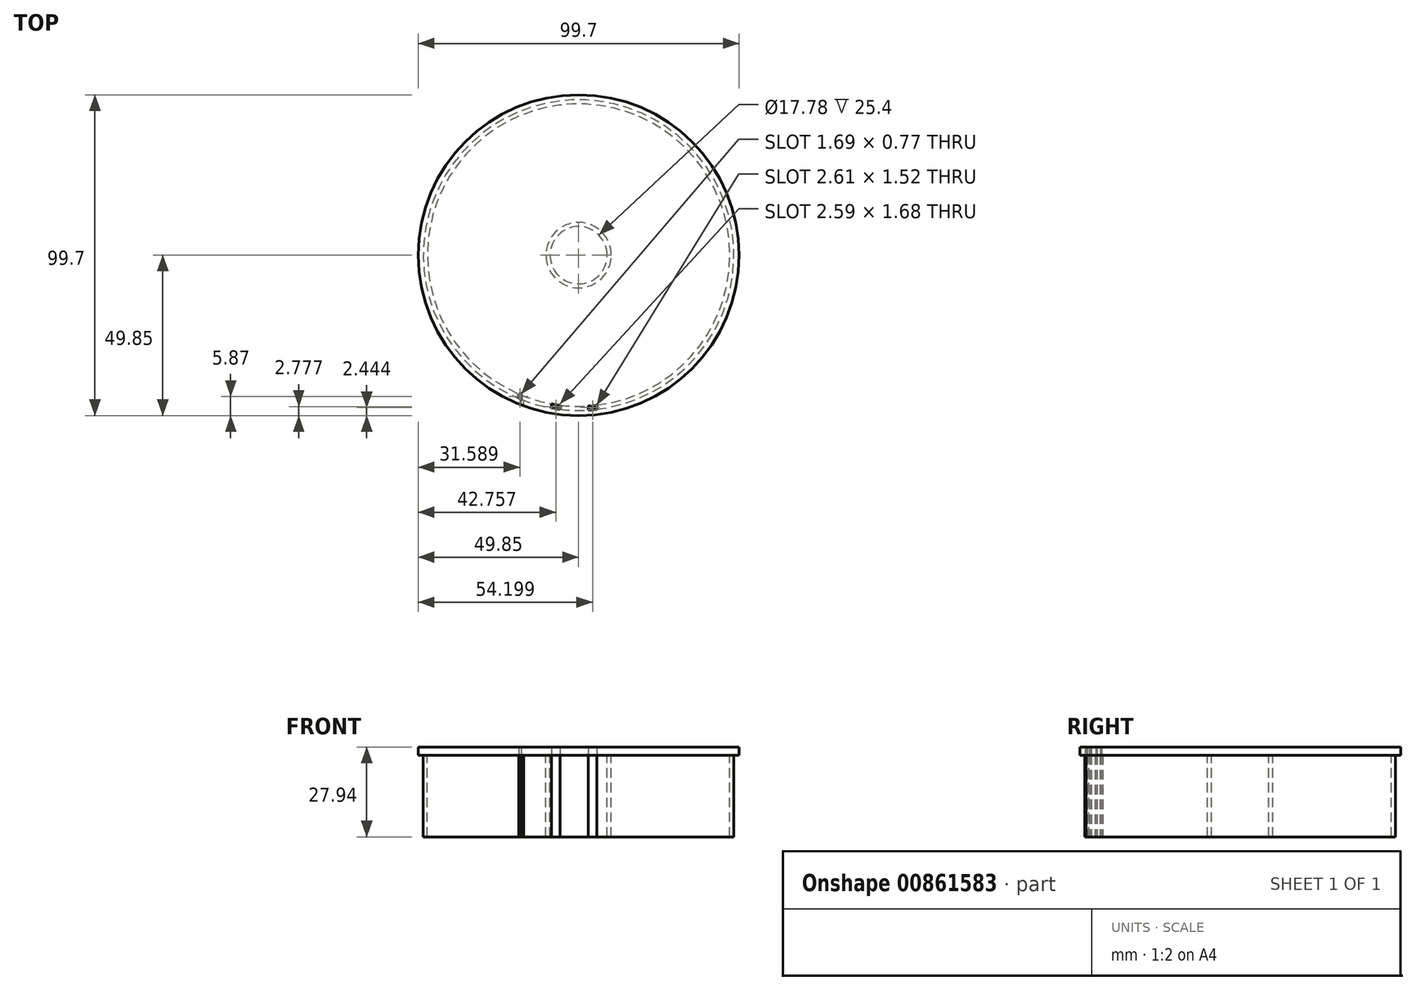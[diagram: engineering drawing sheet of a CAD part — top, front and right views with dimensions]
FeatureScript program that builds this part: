
annotation { "Feature Type Name" : "Feature", "Feature Type Description" : "" }
export const myFeature = defineFeature(function(context is Context, id is Id, definition is map)
    precondition{}
    {
        {
            var Q0;
            Q0=qCreatedBy(makeId("Top.planeOp"),FACE);
            var sketch = newSketch(context, id + "F0", { "sketchPlane" : qUnion([Q0])});
            skCircle(sketch, "E0", {"center": v(0, 0) * mm, "radius": 10.16 * mm});
            skCircle(sketch, "E1", {"center": v(0, 0) * mm, "radius": 48.26 * mm});
            skCircle(sketch, "E2", {"center": v(0, 0) * mm, "radius": 8.9 * mm});
            skCircle(sketch, "E3", {"center": v(0, 0) * mm, "radius": 47 * mm});
            skSolve(sketch);
        }
        {
            var Q0;
            Q0=makeQuery(id+"F0.imprint","IMPRINT",FACE,{"disambiguationData":[TD([[makeQuery(id+"F0.imprint","IMPRINT",EDGE,{"derivedFrom":sQuery(id+"F0.wireOp",EDGE,"E0")}),1.0]])]});
            var Q1;
            Q1=makeQuery(id+"F0.imprint","IMPRINT",FACE,{"disambiguationData":[TD([[makeQuery(id+"F0.imprint","IMPRINT",EDGE,{"derivedFrom":sQuery(id+"F0.wireOp",EDGE,"E1")}),1.0]])]});
            extrude(context, id + "F1", {"entities" : qUnion([Q0, Q1]), "oppositeDirection" : true, "depth" : 25.4 * mm, "offsetDistance" : 25.4 * mm});
        }
        {
            var Q0;
            Q0=qCreatedBy(makeId("Top.planeOp"),FACE);
            var sketch = newSketch(context, id + "F2", { "sketchPlane" : qUnion([Q0])});
            skCircle(sketch, "E4", {"center": v(0, 0) * mm, "radius": 49.85 * mm});
            skSolve(sketch);
        }
        {
            var Q0;
            Q0=makeQuery(id+"F2.imprint","IMPRINT",FACE,{"disambiguationData":[TD([[makeQuery(id+"F2.imprint","IMPRINT",EDGE,{"derivedFrom":sQuery(id+"F2.wireOp",EDGE,"E4")}),1.0]])]});
            extrude(context, id + "F3", {"entities" : qUnion([Q0]), "depth" : 2.54 * mm, "offsetDistance" : 25.4 * mm});
        }
        {
            var Q0;
            Q0=makeQuery(id+"F1.opExtrude","CAP_FACE",FACE,{"disambiguationData":[OSD([sQuery(id+"F0.wireOp",EDGE,"E1"),sQuery(id+"F0.wireOp",EDGE,"E3")])],"isStart":false});
            var sketch = newSketch(context, id + "F4", { "sketchPlane" : qUnion([Q0])});
            skLineSegment(sketch, "E5", {"start": v(-18.64, 44.51) * mm, "end": v(-18.64, 43.13) * mm});
            skLineSegment(sketch, "E6", {"start": v(-17.88, 44.83) * mm, "end": v(-17.88, 43.46) * mm});
            skLineSegment(sketch, "E7", {"start": v(-17.88, 43.46) * mm, "end": v(-18.64, 43.13) * mm});
            skLineSegment(sketch, "E8", {"start": v(-8.39, 47.53) * mm, "end": v(-8.39, 46.23) * mm});
            skLineSegment(sketch, "E9", {"start": v(-8.39, 46.23) * mm, "end": v(-5.8, 46.63) * mm});
            skLineSegment(sketch, "E10", {"start": v(-5.8, 46.63) * mm, "end": v(-5.8, 47.91) * mm});
            skLineSegment(sketch, "E11", {"start": v(-5.8, 47.91) * mm, "end": v(-8.39, 47.53) * mm});
            skLineSegment(sketch, "E12", {"start": v(3.04, 48.16) * mm, "end": v(3.04, 46.9) * mm});
            skLineSegment(sketch, "E13", {"start": v(3.04, 46.9) * mm, "end": v(5.66, 46.65) * mm});
            skLineSegment(sketch, "E14", {"start": v(5.66, 46.65) * mm, "end": v(5.66, 47.93) * mm});
            skLineSegment(sketch, "E15", {"start": v(5.66, 47.93) * mm, "end": v(3.04, 48.16) * mm});
            skSolve(sketch);
        }
        {
            var Q0;
            {var subQ0=sQuery(id+"F4.wireOp",EDGE,"E5");Q0=makeQuery(id+"F4.imprint","IMPRINT",FACE,{"disambiguationData":[TD([[makeQuery(id+"F4.imprint","IMPRINT",EDGE,{"derivedFrom":subQ0}),1.0]])]});}
            var Q1;
            {var subQ0=sQuery(id+"F4.wireOp",EDGE,"E8");Q1=makeQuery(id+"F4.imprint","IMPRINT",FACE,{"disambiguationData":[TD([[makeQuery(id+"F4.imprint","IMPRINT",EDGE,{"derivedFrom":subQ0}),1.0]])]});}
            var Q2;
            {var subQ0=sQuery(id+"F4.wireOp",EDGE,"E12");Q2=makeQuery(id+"F4.imprint","IMPRINT",FACE,{"disambiguationData":[TD([[makeQuery(id+"F4.imprint","IMPRINT",EDGE,{"derivedFrom":subQ0}),1.0]])]});}
            var Q3;
            {var subQ0=sQuery(id+"F4.wireOp",EDGE,"E15");Q3=makeQuery(id+"F4.imprint","IMPRINT",FACE,{"disambiguationData":[TD([[makeQuery(id+"F4.imprint","IMPRINT",EDGE,{"derivedFrom":subQ0}),-1.0]])]});}
            var Q4;
            {var subQ0=sQuery(id+"F4.wireOp",EDGE,"E11");Q4=makeQuery(id+"F4.imprint","IMPRINT",FACE,{"disambiguationData":[TD([[makeQuery(id+"F4.imprint","IMPRINT",EDGE,{"derivedFrom":subQ0}),-1.0]])]});}
            var Q5;
            {var subQ0=sQuery(id+"F4.wireOp",EDGE,"k1nUqgva-zV7j-k8H1-96NG-bMIFicMV9fsw");Q5=makeQuery(id+"F4.imprint","IMPRINT",FACE,{"disambiguationData":[TD([[makeQuery(id+"F4.imprint","IMPRINT",EDGE,{"derivedFrom":subQ0}),-1.0]])]});}
            extrude(context, id + "F5", {"entities" : qUnion([Q0, Q1, Q2, Q3, Q4, Q5]), "operationType" : NewBodyOperationType.REMOVE, "endBound" : BoundingType.THROUGH_ALL, "oppositeDirection" : true, "depth" : 25.4 * mm, "offsetDistance" : 25.4 * mm});
        }
        {
            var Q0;
            {var subQ0=sQuery(id+"F0.wireOp",EDGE,"E1");var subQ1=sQuery(id+"F0.wireOp",EDGE,"E3");Q0=makeQuery(id+"F5.boolean.opBoolean","SPLIT",FACE,{"disambiguationData":[TD([makeQuery(id+"F5.opExtrude","SWEPT_FACE",FACE,{"disambiguationData":[OSD([sQuery(id+"F4.wireOp",EDGE,"E6")])]})])],"derivedFrom":makeQuery(id+"F1.opExtrude","CAP_FACE",FACE,{"disambiguationData":[OSD([subQ0,subQ1])],"isStart":false})});}
            var sketch = newSketch(context, id + "F6", { "sketchPlane" : qUnion([Q0])});
            skLineSegment(sketch, "E16", {"start": v(-17.88, 43.46) * mm, "end": v(-18, 42.7) * mm});
            skLineSegment(sketch, "E17", {"start": v(-18, 42.7) * mm, "end": v(-17.68, 42.7) * mm});
            skLineSegment(sketch, "E18", {"start": v(-17.68, 42.7) * mm, "end": v(-17.68, 43.54) * mm});
            skLineSegment(sketch, "E19", {"start": v(-17.88, 44.83) * mm, "end": v(-17.13, 45.12) * mm});
            skLineSegment(sketch, "E20", {"start": v(-17.88, 46.5) * mm, "end": v(-17.13, 46.8) * mm});
            skLineSegment(sketch, "E21", {"start": v(-17.88, 46.5) * mm, "end": v(-17.88, 44.83) * mm});
            skLineSegment(sketch, "E22", {"start": v(-17.13, 46.8) * mm, "end": v(-17.13, 45.12) * mm});
            skSolve(sketch);
        }
        {
            var Q0;
            {var subQ0=sQuery(id+"F6.wireOp",EDGE,"E16");Q0=makeQuery(id+"F6.imprint","IMPRINT",FACE,{"disambiguationData":[TD([[makeQuery(id+"F6.imprint","IMPRINT",EDGE,{"derivedFrom":subQ0}),1.0]])]});}
            var Q1;
            Q1=makeQuery(id+"F6.imprint","IMPRINT",FACE,{"disambiguationData":[TD([[makeQuery(id+"F6.imprint","IMPRINT",EDGE,{"derivedFrom":sQuery(id+"F6.wireOp",EDGE,"E19")}),1.0]])]});
            extrude(context, id + "F7", {"entities" : qUnion([Q0, Q1]), "oppositeDirection" : true, "depth" : 25.4 * mm, "offsetDistance" : 25.4 * mm});
        }
    });
